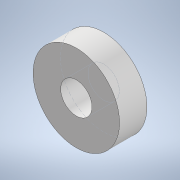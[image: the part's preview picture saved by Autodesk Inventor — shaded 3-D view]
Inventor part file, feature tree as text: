
AUTODESK INVENTOR PART (.ipt)
format: ipt  version: 2022 (Build 260153070, 153G)  size: 98,816 bytes
history: native  units: mm
features: extrude x1, sketch x1
ambient origin geometry x8: Origin, YZ Plane, XZ Plane, XY Plane, X Axis, Y Axis, Z Axis, Center Point
bodies: Solid1 (feature_tree)
feature tree (2):
  extrude  "Extrusion1"  Depth=7.0mm
  sketch  "Sketch1"  dims[d0=22.1mm d1=8.0mm d2=7.0mm d3=0.0mm]
